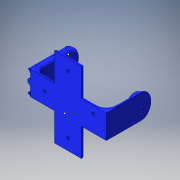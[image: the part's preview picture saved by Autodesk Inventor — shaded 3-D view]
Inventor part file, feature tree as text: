
AUTODESK INVENTOR PART (.ipt)
format: ipt  version: 2016 (Build 200138000, 138)  size: 602,112 bytes
history: native  units: in
note: dims shown in document units (in); Inventor stores cm internally (conversion verified against a paired STEP export)
features: sketch x13, extrude x12, fillet x12, hole x2
ambient origin geometry x8: Origin, YZ Plane, XZ Plane, XY Plane, X Axis, Y Axis, Z Axis, Center Point
bodies: Solid1 (feature_tree)
feature tree (39):
  extrude  "Extrusion1"  Depth=0.5197in
  extrude  "Extrusion3"  Depth=0.0787in
  sketch  "Sketch5"  dims[d9=0.9449in d10=0.0in d11=0.2835in]
  extrude  "Extrusion4"  Depth=0.2835in
  extrude  "Extrusion5"  Depth=0.2598in
  fillet  "Fillet1"  Radius=0.2598in
  fillet  "Fillet4"  Radius=0.5197in
  fillet  "Fillet5"  Radius=0.3622in
  fillet  "Fillet6"  Radius=0.1437in
  fillet  "Fillet7"  Radius=0.2224in
  extrude  "Extrusion6"  Depth=0.0787in
  sketch  "Sketch9"  dims[d24=0.0787in d25=0.0in d27=0.0787in]
  extrude  "Extrusion7"  Depth=0.0197in
  fillet  "Fillet10"  Radius=0.0197in
  fillet  "Fillet11"  Radius=0.0394in
  sketch  "Sketch10"  dims[d28=0.0787in d29=0.0in d30=0.1969in d33=0.0197in d34=0.0394in]
  extrude  "Extrusion8"  Depth=0.0197in
  extrude  "Extrusion10"  Depth=0.9449in TaperAngle=0.0deg
  extrude  "Extrusion11"  Depth=0.2598in
  sketch  "Sketch17"  dims[d43=0.2598in d44=0.2598in]
  hole  "Hole2"  [1 undecoded]
  fillet  "Fillet18"  Radius=0.1772in
  extrude  "Extrusion12"  Depth=0.0197in
  extrude  "Extrusion13"  Depth=0.1181in TaperAngle=0.0deg
  fillet  "Fillet22"  Radius=0.5838in
  hole  "Hole3"  [1 undecoded]
  extrude  "Extrusion15"  Depth=0.0197in TaperAngle=0.0deg
  fillet  "Fillet24"  Radius=0.5349in
  fillet  "Fillet25"  Radius=0.6043in
  fillet  "Fillet26"  Radius=0.1181in
  sketch  "Sketch21"  dims[d83=0.5349in d84=0.5349in d85=0.6043in d86=0.0in d87=0.5349in d88=0.6043in d89=0.0in d90=0.0591in d91=0.2362in d92=0.1575in d93=0.0787in d94=90.0deg d95=0.315in d96=0.8108in d98=0.1181in d99=0.5591in d100=0.5591in d101=0.5591in d103=0.4291in d104=0.0in d106=0.0591in d107=0.4291in d108=0.0in d111=0.0748in d112=0.0591in d113=0.2362in d114=0.1575in d115=0.0787in d116=90.0deg d117=0.315in d118=0.8108in d124=0.0591in d125=0.0591in d126=0.0in d127=0.0787in d128=0.0197in d129=0.0197in d130=0.2362in d131=0.2362in d132=0.2919in d133=0.2919in d134=0.2919in d135=0.2919in d136=0.2756in d137=0.1575in]
  sketch  "Sketch1"  dims[d0=1.6535in d1=0.5197in]
  sketch  "Sketch4"  dims[d2=0.0787in d3=0.0in d8=0.0787in]
  sketch  "Sketch7"  dims[d12=0.2598in d13=0.2598in d14=0.2598in d15=0.5197in d16=0.3622in d17=0.1437in d19=0.2224in]
  sketch  "Sketch15"  dims[d35=0.0394in d36=0.0197in]
  sketch  "Sketch16"  dims[d37=0.0787in d38=0.9449in d39=0.0in]
  sketch  "Sketch18"  dims[d45=0.2598in d46=0.1181in d47=0.1772in d48=0.0in]
  sketch  "Sketch19"  dims[d49=0.0394in d50=0.0197in]
  sketch  "Sketch20"  dims[d51=0.1181in d52=0.1181in d53=0.0in d82=0.5838in]
note: 2 required parameter values undecoded (feature->parameter linkage not recoverable at this tier; creation-order binding heuristic only, values carry confidence <= 0.55)
